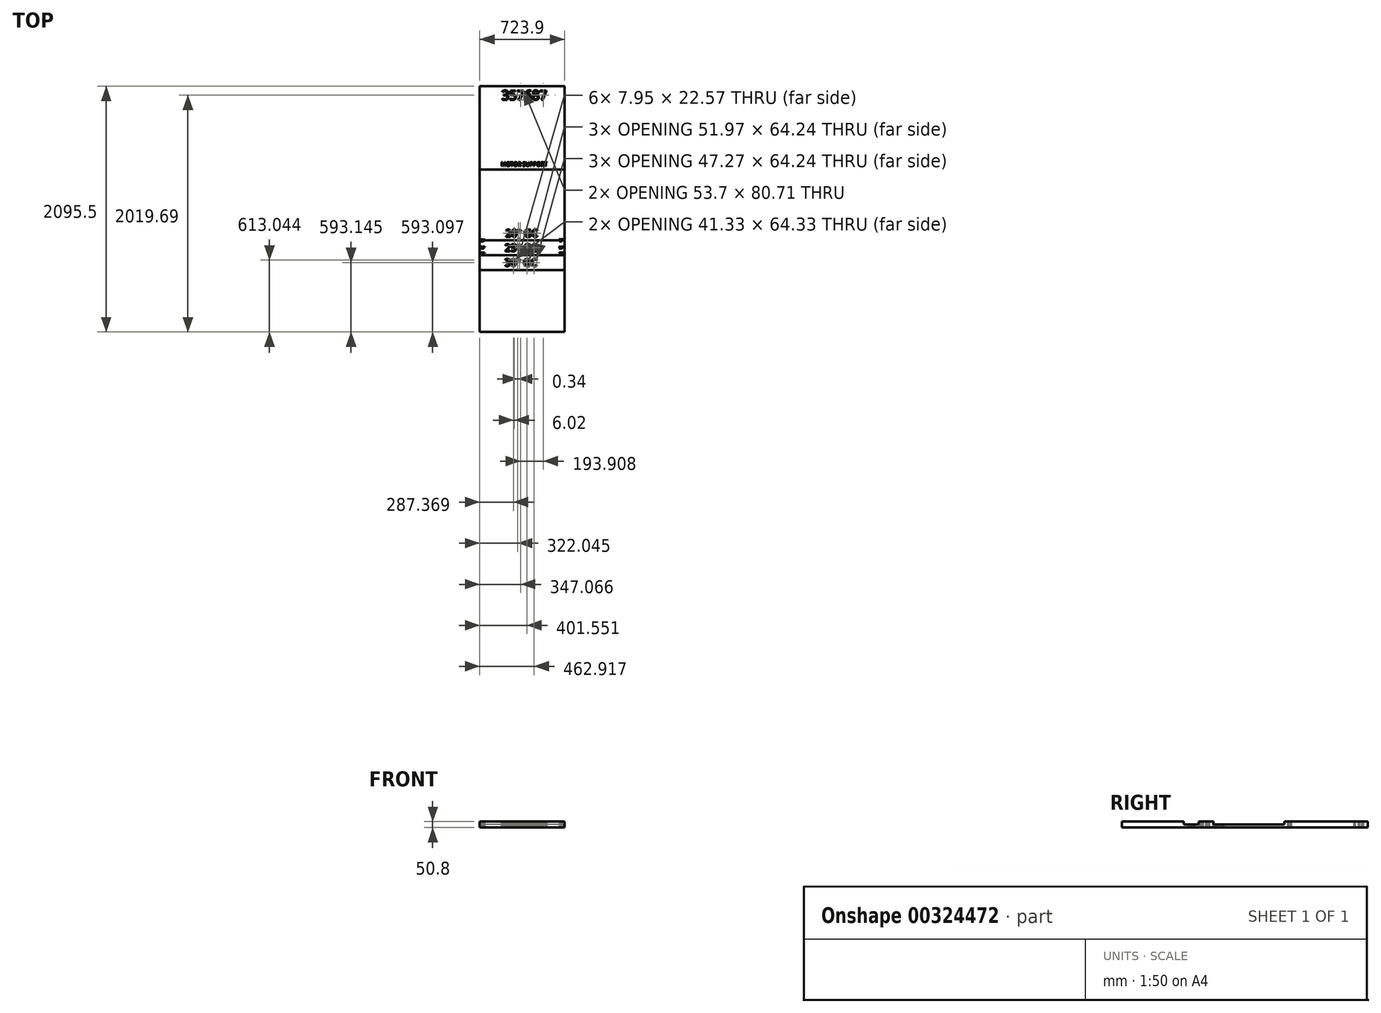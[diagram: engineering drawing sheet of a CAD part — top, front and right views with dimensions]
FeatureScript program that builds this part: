
annotation { "Feature Type Name" : "Feature", "Feature Type Description" : "" }
export const myFeature = defineFeature(function(context is Context, id is Id, definition is map)
    precondition{}
    {
        {
            var Q0;
            Q0=qCreatedBy(makeId("Top.planeOp"),FACE);
            var sketch = newSketch(context, id + "F0", { "sketchPlane" : qUnion([Q0])});
            skLineSegment(sketch, "E0.bottom", {"start": v(-357.08, 1609.6) * mm, "end": v(366.82, 1609.6) * mm});
            skLineSegment(sketch, "E0.top", {"start": v(-357.08, -485.9) * mm, "end": v(366.82, -485.9) * mm});
            skLineSegment(sketch, "E0.left", {"start": v(-357.08, 1609.6) * mm, "end": v(-357.08, -485.9) * mm});
            skLineSegment(sketch, "E0.right", {"start": v(366.82, 1609.6) * mm, "end": v(366.82, -485.9) * mm});
            skSolve(sketch);
        }
        {
            var Q0;
            Q0 = qSketchRegion(id + "F0", true);
            extrude(context, id + "F1", {"entities" : qUnion([Q0]), "depth" : 25.4 * mm});
        }
        {
            var Q0;
            Q0=makeQuery(id+"F1.opExtrude","CAP_FACE",FACE,{"disambiguationData":[OSD([sQuery(id+"F0.wireOp",EDGE,"E0.bottom"),sQuery(id+"F0.wireOp",EDGE,"E0.top"),sQuery(id+"F0.wireOp",EDGE,"E0.left"),sQuery(id+"F0.wireOp",EDGE,"E0.right")])],"isStart":false});
            var sketch = newSketch(context, id + "F2", { "sketchPlane" : qUnion([Q0])});
            skLineSegment(sketch, "E1", {"start": v(366.82, 295.15) * mm, "end": v(-357.08, 295.15) * mm});
            skLineSegment(sketch, "E2", {"start": v(-357.08, 295.15) * mm, "end": v(-357.08, 168.15) * mm});
            skLineSegment(sketch, "E3", {"start": v(-357.08, 168.15) * mm, "end": v(366.82, 168.15) * mm});
            skLineSegment(sketch, "E4", {"start": v(366.82, 168.15) * mm, "end": v(366.82, 295.15) * mm});
            skLineSegment(sketch, "E5", {"start": v(-357.08, 41.15) * mm, "end": v(366.82, 41.15) * mm});
            skLineSegment(sketch, "E6", {"start": v(366.82, 41.15) * mm, "end": v(366.82, -485.9) * mm});
            skLineSegment(sketch, "E7", {"start": v(366.82, -485.9) * mm, "end": v(-357.08, -485.9) * mm});
            skLineSegment(sketch, "E8", {"start": v(-357.08, -485.9) * mm, "end": v(-357.08, 41.15) * mm});
            skLineSegment(sketch, "E9", {"start": v(-357.08, 1609.6) * mm, "end": v(366.82, 1609.6) * mm});
            skLineSegment(sketch, "E10", {"start": v(366.82, 1609.6) * mm, "end": v(366.82, 898.4) * mm});
            skLineSegment(sketch, "E11", {"start": v(366.82, 898.4) * mm, "end": v(-357.08, 898.4) * mm});
            skLineSegment(sketch, "E12", {"start": v(-357.08, 898.4) * mm, "end": v(-357.08, 1609.6) * mm});
            skSolve(sketch);
        }
        {
            var Q0;
            Q0 = qSketchRegion(id + "F2", true);
            extrude(context, id + "F3", {"entities" : qUnion([Q0]), "operationType" : NewBodyOperationType.ADD, "depth" : 25.4 * mm});
        }
        {
            var Q0;
            {var subQ0=sQuery(id+"F0.wireOp",EDGE,"E0.left");var subQ1=sQuery(id+"F0.wireOp",EDGE,"E0.right");Q0=makeQuery(id+"F3.boolean.opBoolean","SPLIT",FACE,{"disambiguationData":[TD([makeQuery(id+"F3.opExtrude","SWEPT_FACE",FACE,{"disambiguationData":[OSD([sQuery(id+"F2.wireOp",EDGE,"E1")])]})])],"derivedFrom":makeQuery(id+"F1.opExtrude","CAP_FACE",FACE,{"disambiguationData":[OSD([sQuery(id+"F0.wireOp",EDGE,"E0.bottom"),sQuery(id+"F0.wireOp",EDGE,"E0.top"),subQ0,subQ1])],"isStart":false})});}
            var sketch = newSketch(context, id + "F4", { "sketchPlane" : qUnion([Q0])});
            skText(sketch, "E13", { "text": "357687", "fontName": "OpenSans-Regular.ttf"});
            skText(sketch, "E14", { "text": "MOTOR SUPPORT", "fontName": "OpenSans-Regular.ttf"});
            skText(sketch, "E15", { "text": "20\" GC", "fontName": "OpenSans-Regular.ttf"});
            skText(sketch, "E16", { "text": "25\" GC", "fontName": "OpenSans-Regular.ttf"});
            skText(sketch, "E17", { "text": "30\" GC", "fontName": "OpenSans-Regular.ttf"});
            const initialGuessF4  = {"E13": [-0.17133, 1.49343, 1, 0, 0.0814], "E14": [-0.17658, 0.92892, 1, 0, 0.03413], "E15": [-0.13876, 0.32547, 1, 0, 0.06302], "E16": [-0.14444, 0.20108, 1, 0, 0.06302], "E17": [-0.14478, 0.07594, 1, 0, 0.06302]};
            skSetInitialGuess(sketch, initialGuessF4);
            skSolve(sketch);
        }
        {
            var Q0;
            Q0 = qSketchRegion(id + "F4", true);
            extrude(context, id + "F5", {"entities" : qUnion([Q0]), "operationType" : NewBodyOperationType.REMOVE, "oppositeDirection" : true, "depth" : 25.4 * mm, "hasSecondDirection" : true, "secondDirectionOppositeDirection" : false, "secondDirectionDepth" : 25.4 * mm});
        }
        {
            var Q0;
            {var subQ5=sQuery(id+"F0.wireOp",EDGE,"E0.right");var subQ8=makeQuery(id+"F3.opExtrude","SWEPT_FACE",FACE,{"disambiguationData":[OSD([sQuery(id+"F2.wireOp",EDGE,"E1")])]});var subQ10=sQuery(id+"F0.wireOp",EDGE,"E0.left");var subQ11=makeQuery(id+"F1.opExtrude","SWEPT_FACE",FACE,{"disambiguationData":[OSD([subQ10])]});Q0=makeQuery(id+"F5.boolean.opBoolean","SPLIT",FACE,{"disambiguationData":[TD([subQ11])],"derivedFrom":makeQuery(id+"F3.boolean.opBoolean","SPLIT",FACE,{"disambiguationData":[TD([subQ8])],"derivedFrom":makeQuery(id+"F1.opExtrude","CAP_FACE",FACE,{"disambiguationData":[OSD([sQuery(id+"F0.wireOp",EDGE,"E0.bottom"),sQuery(id+"F0.wireOp",EDGE,"E0.top"),subQ10,subQ5])],"isStart":false})})});}
            var sketch = newSketch(context, id + "F6", { "sketchPlane" : qUnion([Q0])});
            skText(sketch, "E18", { "text": "25\"", "fontName": "OpenSans-Regular.ttf"});
            skText(sketch, "E19", { "text": "30\"", "fontName": "OpenSans-Regular.ttf"});
            skText(sketch, "E20", { "text": "20\"", "fontName": "OpenSans-Regular.ttf"});
            skText(sketch, "E21", { "text": "25\"", "fontName": "OpenSans-Regular.ttf"});
            skText(sketch, "E22", { "text": "30\"", "fontName": "OpenSans-Regular.ttf"});
            skText(sketch, "E23", { "text": "20\"", "fontName": "OpenSans-Regular.ttf"});
            const initialGuessF6  = {"E18": [0.31901, 0.28833, 1, 0, 0.0164], "E19": [0.3189, 0.22555, 1, 0, 0.0164], "E20": [0.31915, 0.176, 1, 0, 0.0164], "E21": [-0.34706, 0.2881, 1, 0, 0.0164], "E22": [-0.34716, 0.22532, 1, 0, 0.0164], "E23": [-0.34692, 0.17577, 1, 0, 0.0164]};
            skSetInitialGuess(sketch, initialGuessF6);
            skSolve(sketch);
        }
        {
            var Q0;
            Q0 = qSketchRegion(id + "F6", true);
            extrude(context, id + "F7", {"entities" : qUnion([Q0]), "operationType" : NewBodyOperationType.REMOVE, "depth" : 25.4 * mm, "hasSecondDirection" : true, "secondDirectionOppositeDirection" : true, "secondDirectionDepth" : 25.4 * mm});
        }
    });
